# Revit family: Bottle_Filler-Haws-3690-Outdoor_Wall_Mounted-TW3-CS2
name_source: partatom
category: Plumbing Fixtures
units: mm (PartAtom-declared; Revit-internal decimal feet)

## family parameters
Always vertical = Yes
Cut with Voids When Loaded = No
OmniClass Number = 23.65.70.14.11
OmniClass Title = Drinking Fountains/Coolers
Part Type = Normal
Room Calculation Point = No
Round Connector Dimension = Use Diameter
Shared = No
Work Plane-Based = No

## types (1)
- Bottle Filler
    Assembly Code = D2010800
    CD_Depth = 0' - 10 1/16"
    CD_Finish = Metal-Powder_Coat-Haws-Stainless_Steel-Matte_Silver
    CD_Height = 2' - 3 1/2"
    CD_Install Documentation = https://www.hawsco.com
    CD_Microsite = https://www.caddetails.com
    CD_Product Documentation Link = https://www.hawsco.com
    CD_Product Page URL = https://www.hawsco.com
    CD_Sanitary Description = 3690 Connector
    CD_Warranty = https://www.hawsco.com
    CD_Width = 0' - 10"
    Default Elevation = 2' - 3"
    Description = Outdoor Wall Mounted Bottle Filler
    Manufacturer = Haws Corporation
    Model = 3690 Config WM
    Type Comments = ADA Compliant Bottle Filler
    URL = https://www.hawsco.com

## geometry (parser evidence)
native form markers: Sweep x3
no freeform markers — native parametric forms only
